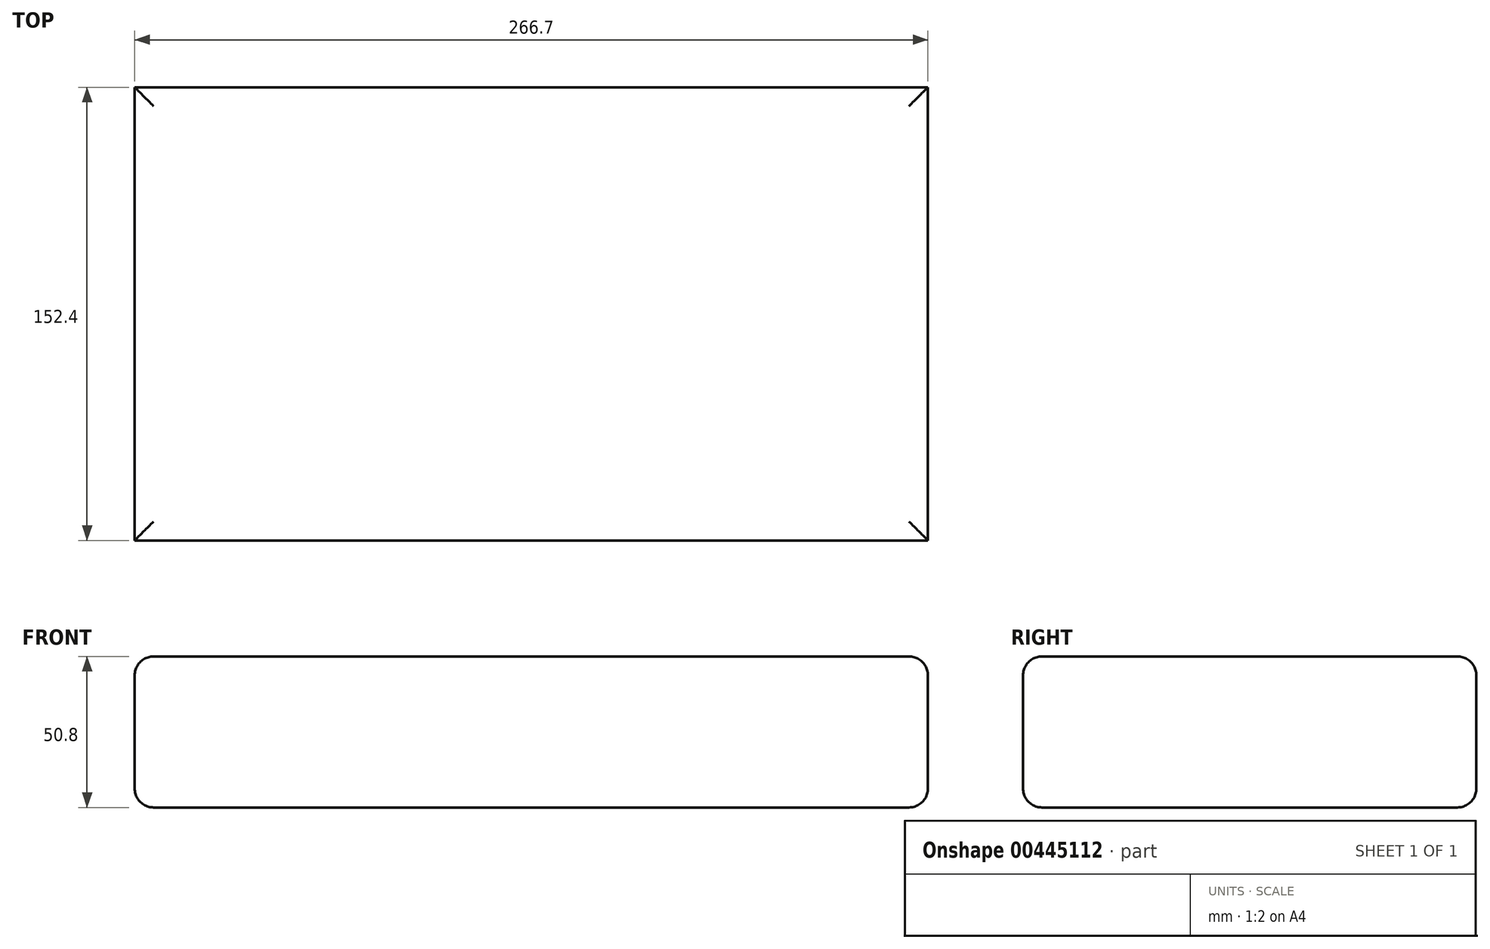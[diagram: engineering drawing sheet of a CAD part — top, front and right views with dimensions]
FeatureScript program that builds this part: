
annotation { "Feature Type Name" : "Feature", "Feature Type Description" : "" }
export const myFeature = defineFeature(function(context is Context, id is Id, definition is map)
    precondition{}
    {
        {
            var Q0;
            Q0=qCreatedBy(makeId("Top.planeOp"),FACE);
            var sketch = newSketch(context, id + "F0", { "sketchPlane" : qUnion([Q0])});
            skLineSegment(sketch, "E0.bottom", {"start": v(133.35, 76.2) * mm, "end": v(-133.35, 76.2) * mm});
            skLineSegment(sketch, "E0.top", {"start": v(133.35, -76.2) * mm, "end": v(-133.35, -76.2) * mm});
            skLineSegment(sketch, "E0.left", {"start": v(133.35, 76.2) * mm, "end": v(133.35, -76.2) * mm});
            skLineSegment(sketch, "E0.right", {"start": v(-133.35, 76.2) * mm, "end": v(-133.35, -76.2) * mm});
            skPoint(sketch, "E0.middle", {"position": v(0, 0) * mm});
            skSolve(sketch);
        }
        {
            var Q0;
            Q0=makeQuery(id+"F0.imprint","IMPRINT",FACE,{"disambiguationData":[TD([[makeQuery(id+"F0.imprint","IMPRINT",EDGE,{"derivedFrom":sQuery(id+"F0.wireOp",EDGE,"E0.bottom")}),1.0]])]});
            extrude(context, id + "F1", {"entities" : qUnion([Q0]), "depth" : 50.8 * mm});
        }
        {
            var Q0;
            Q0=makeQuery(id+"F1.opExtrude","CAP_FACE",FACE,{"disambiguationData":[OSD([sQuery(id+"F0.wireOp",EDGE,"E0.bottom"),sQuery(id+"F0.wireOp",EDGE,"E0.top"),sQuery(id+"F0.wireOp",EDGE,"E0.left"),sQuery(id+"F0.wireOp",EDGE,"E0.right")])],"isStart":false});
            var sketch = newSketch(context, id + "F2", { "sketchPlane" : qUnion([Q0])});
            skCircle(sketch, "E1", {"center": v(0, 0) * mm, "radius": 19.05 * mm});
            skLineSegment(sketch, "E2", {"start": v(19.05, 0) * mm, "end": v(44.45, 0) * mm});
            skLineSegment(sketch, "E3", {"start": v(-19.05, 0) * mm, "end": v(-44.45, 0) * mm});
            skLineSegment(sketch, "E4", {"start": v(44.45, 0) * mm, "end": v(63.5, 0) * mm});
            skLineSegment(sketch, "E5", {"start": v(-44.45, 0) * mm, "end": v(-63.5, 0) * mm});
            skCircle(sketch, "E6", {"center": v(-63.5, 0) * mm, "radius": 19.05 * mm});
            skCircle(sketch, "E7", {"center": v(63.5, 0) * mm, "radius": 19.05 * mm});
            skSolve(sketch);
        }
        {
            var Q0;
            Q0=makeQuery(id+"F1.opExtrude","CAP_EDGE",EDGE,{"disambiguationData":[OSD([sQuery(id+"F0.wireOp",EDGE,"E0.bottom")])],"isStart":false});
            var Q1;
            Q1=makeQuery(id+"F1.opExtrude","CAP_EDGE",EDGE,{"disambiguationData":[OSD([sQuery(id+"F0.wireOp",EDGE,"E0.left")])],"isStart":false});
            var Q2;
            Q2=makeQuery(id+"F1.opExtrude","CAP_EDGE",EDGE,{"disambiguationData":[OSD([sQuery(id+"F0.wireOp",EDGE,"E0.top")])],"isStart":false});
            var Q3;
            Q3=makeQuery(id+"F1.opExtrude","CAP_EDGE",EDGE,{"disambiguationData":[OSD([sQuery(id+"F0.wireOp",EDGE,"E0.right")])],"isStart":true});
            var Q4;
            Q4=makeQuery(id+"F1.opExtrude","CAP_EDGE",EDGE,{"disambiguationData":[OSD([sQuery(id+"F0.wireOp",EDGE,"E0.right")])],"isStart":false});
            var Q5;
            Q5=makeQuery(id+"F1.opExtrude","CAP_EDGE",EDGE,{"disambiguationData":[OSD([sQuery(id+"F0.wireOp",EDGE,"E0.bottom")])],"isStart":true});
            var Q6;
            Q6=makeQuery(id+"F1.opExtrude","CAP_EDGE",EDGE,{"disambiguationData":[OSD([sQuery(id+"F0.wireOp",EDGE,"E0.left")])],"isStart":true});
            var Q7;
            Q7=makeQuery(id+"F1.opExtrude","CAP_EDGE",EDGE,{"disambiguationData":[OSD([sQuery(id+"F0.wireOp",EDGE,"E0.top")])],"isStart":true});
            fillet(context, id + "F3", {"entities" : qUnion([Q0, Q1, Q2, Q3, Q4, Q5, Q6, Q7]), "radius" : 6.35 * mm, "tangentPropagation" : true, "allowEdgeOverflow" : false});
        }
    });
